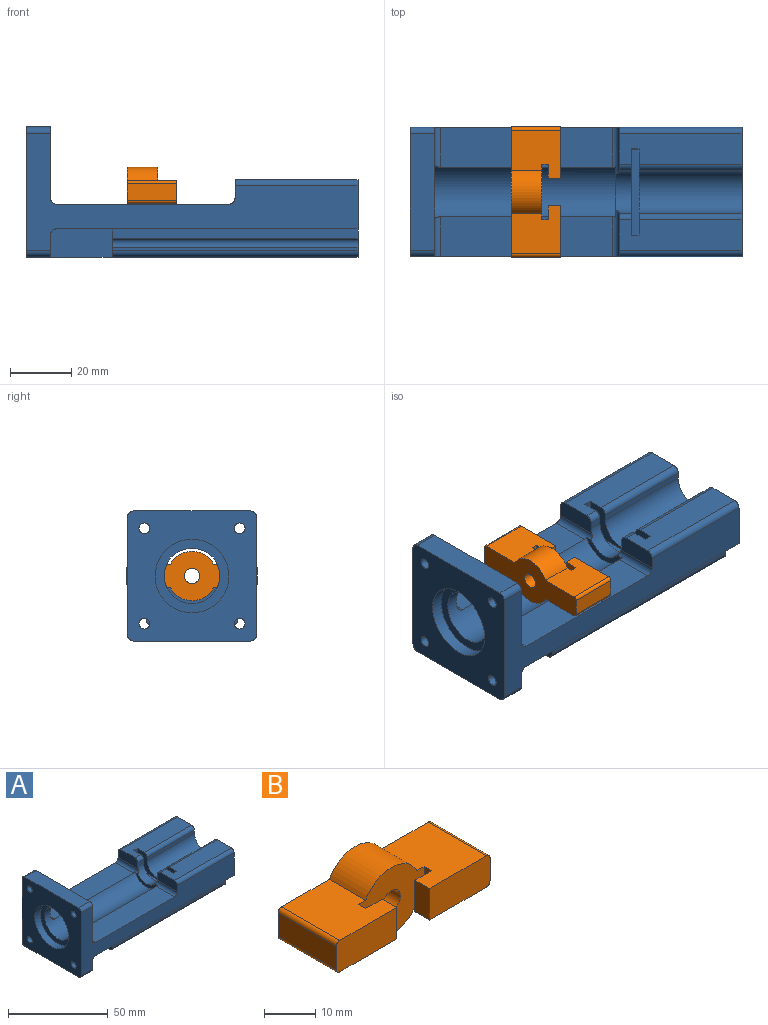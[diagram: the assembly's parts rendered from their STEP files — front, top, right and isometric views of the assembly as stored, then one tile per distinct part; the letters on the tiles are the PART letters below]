
ASSEMBLY  parts=2 mates=1
PART A: 73 faces, bbox 108x42x42.3 mm
  f0: plane 56x12.94mm, normal (0,0,1), area 724.5mm2, adj f8,f9,f27,f70
  f1: plane 56x12.94mm, normal (0,0,1), area 724.5mm2, adj f6,f7,f28,f70
  f2: plane 4x0.52mm, normal (0,0,-1), area 2.1mm2, adj f5,f21,f34,f72
  f3: plane 4x0.52mm, normal (0,0,-1), area 2.1mm2, adj f4,f21,f34,f72
  f4: plane 4x0.59mm, normal (0,1,0), area 2.4mm2, adj f3,f21,f34,f70
  f5: plane 4x0.59mm, normal (0,-1,0), area 2.4mm2, adj f2,f21,f34,f70
  f6: cylinder r=2mm len=15.08mm, axis (0,-1,0), area 44.2mm2, adj f1,f17,f20,f28,f70,f71
  f7: cylinder r=2mm len=12.94mm, axis (0,-1,0), area 39.5mm2, adj f1,f21,f28,f70
  f8: cylinder r=2mm len=15.08mm, axis (0,-1,0), area 44.2mm2, adj f0,f17,f19,f27,f70,f71
  f9: cylinder r=2mm len=12.94mm, axis (0,-1,0), area 39.5mm2, adj f0,f21,f27,f70
  f10: plane 98.02x10.18mm, normal (0,0,-1), area 677.5mm2, adj f12,f22,f28,f48,f50,f52,f53,f54
  f11: plane 11.8x7.15mm, normal (1,0,0), area 74.2mm2, adj f25,f27,f31,f51,f61,f63,f67
  f12: plane 9.15x4.18mm, normal (-1,0,0), area 34.4mm2, adj f10,f25,f46,f47,f48,f50,f56
  f13: plane 98.02x11.8mm, normal (0,0,-1), area 706.7mm2, adj f22,f27,f43,f49,f51,f61,f62,f63
  f14: plane 40x10mm, normal (0,0,1), area 387.5mm2, adj f19,f22,f38,f40,f41,f57,f59,f69
  f15: plane 40x10mm, normal (0,0,1), area 387.5mm2, adj f20,f22,f38,f39,f40,f58,f60,f66
  f16: plane 4x2mm, normal (0,1,0), area 8mm2, adj f17,f19,f40,f59
  f17: cylinder r=7mm len=14mm, axis (-1,0,0), area 103.2mm2, adj f6,f8,f16,f18,f19,f20,f40,f71
  f18: plane 4x2mm, normal (0,-1,0), area 8mm2, adj f17,f20,f40,f60
  f19: plane 14.29x6mm, normal (-1,0,0), area 82.5mm2, adj f8,f14,f16,f17,f27,f59,f69
  f20: plane 14.29x6mm, normal (-1,0,0), area 82.5mm2, adj f6,f15,f17,f18,f28,f60,f66
  f21: plane 42x23.15mm, normal (1,0,0), area 788.1mm2, adj f2,f3,f4,f5,f7,f9,f23,f27
  f22: plane 42x25.15mm, normal (1,0,0), area 802.4mm2, adj f10,f13,f14,f15,f25,f27,f28,f35
  f23: plane 38x8mm, normal (0,0,1), area 304mm2, adj f21,f24,f65,f68
  f24: plane 42.3x42mm, normal (-1,0,0), area 1282.3mm2, adj f23,f25,f27,f28,f29,f30,f31,f32
  f25: plane 108x38mm, normal (0,0,-1), area 2784.4mm2, adj f11,f12,f22,f24,f26,f49,f50,f51
  f26: plane 10.18x7.15mm, normal (1,0,0), area 62.6mm2, adj f25,f28,f32,f50,f52,f54,f64
  f27: plane 108x38.3mm, normal (0,-1,0), area 1349mm2, adj f0,f8,f9,f11,f13,f19,f21,f22
  f28: plane 108x38.3mm, normal (0,1,0), area 1349mm2, adj f1,f6,f7,f10,f20,f21,f22,f24
  f29: cylinder r=1.75mm len=8mm, axis (-1,0,0), area 88mm2, adj f21,f24
  f30: cylinder r=1.75mm len=8mm, axis (-1,0,0), area 88mm2, adj f21,f24
  f31: cylinder r=1.75mm len=8mm, axis (-1,0,0), area 88mm2, adj f11,f24,f62
  f32: cylinder r=1.75mm len=8mm, axis (-1,0,0), area 88mm2, adj f24,f26,f53
  f33: cylinder r=12mm len=24mm, axis (-1,0,0), area 301.6mm2, adj f24,f34
  f34: plane 24x24mm, normal (-1,0,0), area 197.6mm2, adj f2,f3,f4,f5,f33,f70,f72
  f35: plane 33.5x2mm, normal (0,1,0), area 67mm2, adj f22,f36,f38,f57
  f36: cylinder r=7mm len=33.5mm, axis (-1,0,0), area 736.7mm2, adj f22,f35,f37,f38
  f37: plane 33.5x2mm, normal (0,-1,0), area 67mm2, adj f22,f36,f38,f58
  f38: plane 28x12mm, normal (-1,0,0), area 201.3mm2, adj f14,f15,f35,f36,f37,f39,f41,f42
  f39: plane 12x2.5mm, normal (0,-1,0), area 30mm2, adj f15,f38,f40,f42
  f40: plane 28x12mm, normal (1,0,0), area 201.3mm2, adj f14,f15,f16,f17,f18,f39,f41,f42
  f41: plane 12x2.5mm, normal (0,1,0), area 30mm2, adj f14,f38,f40,f42
  f42: plane 28x2.5mm, normal (0,0,1), area 70mm2, adj f38,f39,f40,f41
  f43: plane 80x3.18mm, normal (0,-1,0), area 254.6mm2, adj f13,f22,f44,f49
  f44: cylinder r=1.5mm len=80mm, axis (1,0,0), area 300.5mm2, adj f22,f43,f45,f49
  f45: plane 80x1.12mm, normal (0,-1,0), area 89.9mm2, adj f22,f44,f49,f55
  f46: plane 80x1.12mm, normal (0,1,0), area 89.9mm2, adj f12,f22,f47,f56
  f47: cylinder r=1.5mm len=80mm, axis (1,0,0), area 300.5mm2, adj f12,f22,f46,f48
  f48: plane 80x3.18mm, normal (0,1,0), area 254.6mm2, adj f10,f12,f22,f47
  f49: plane 9.15x5.8mm, normal (-1,0,0), area 49.3mm2, adj f13,f25,f43,f44,f45,f51,f55
  f50: plane 20x9.15mm, normal (0,1,0), area 182.1mm2, adj f10,f12,f25,f26,f54
  f51: plane 20x9.15mm, normal (0,-1,0), area 182.1mm2, adj f11,f13,f25,f49,f61
  f52: cylinder r=2mm len=4.6mm, axis (0,-1,0), area 14.4mm2, adj f10,f26,f28,f53
  f53: bspline ~2.27x2.16mm, area 5.4mm2, adj f10,f32,f52,f54
  f54: cylinder r=2mm len=3.78mm, axis (0,-1,0), area 11.9mm2, adj f10,f26,f50,f53
  f55: cylinder r=2mm len=80mm, axis (1,0,0), area 251.3mm2, adj f22,f25,f45,f49
  f56: cylinder r=2mm len=80mm, axis (-1,0,0), area 251.3mm2, adj f12,f22,f25,f46
  f57: cylinder r=2mm len=33.5mm, axis (-1,0,0), area 105.2mm2, adj f14,f22,f35,f38
  f58: cylinder r=2mm len=33.5mm, axis (1,0,0), area 105.2mm2, adj f15,f22,f37,f38
  f59: cylinder r=2mm len=4mm, axis (-1,0,0), area 12.6mm2, adj f14,f16,f19,f40
  f60: cylinder r=2mm len=4mm, axis (1,0,0), area 12.6mm2, adj f15,f18,f20,f40
  f61: cylinder r=2mm len=5.4mm, axis (0,-1,0), area 17mm2, adj f11,f13,f51,f62
  f62: bspline ~2.27x2.16mm, area 5.4mm2, adj f13,f31,f61,f63
  f63: cylinder r=2mm len=4.6mm, axis (0,-1,0), area 14.4mm2, adj f11,f13,f27,f62
  f64: cylinder r=2mm len=8mm, axis (1,0,0), area 25.1mm2, adj f24,f25,f26,f28
  f65: cylinder r=2mm len=8mm, axis (-1,0,0), area 25.1mm2, adj f21,f23,f24,f28
  f66: cylinder r=2mm len=40mm, axis (-1,0,0), area 125.7mm2, adj f15,f20,f22,f28
  f67: cylinder r=2mm len=8mm, axis (-1,0,0), area 25.1mm2, adj f11,f24,f25,f27
  f68: cylinder r=2mm len=8mm, axis (1,0,0), area 25.1mm2, adj f21,f23,f24,f27
  f69: cylinder r=2mm len=40mm, axis (1,0,0), area 125.7mm2, adj f14,f19,f22,f27
  f70: cylinder r=9mm len=63mm, axis (-1,0,0), area 1343.3mm2, adj f0,f1,f4,f5,f6,f7,f8,f9
  f71: plane 16.38x5.27mm, normal (-1,0,0), area 34.7mm2, adj f6,f8,f17,f70
  f72: cylinder r=9mm len=12.96mm, axis (-1,0,0), area 57.9mm2, adj f2,f3,f21,f34
PART B: 23 faces, bbox 42.3x16x16 mm
  f0: plane 16x15.65mm, normal (0,0,1), area 215.7mm2, adj f2,f8,f9,f10,f11,f12,f19,f21
  f1: plane 16x15.65mm, normal (0,0,-1), area 215.7mm2, adj f2,f8,f9,f10,f11,f12,f17,f20
  f2: plane 42.3x16mm, normal (0,1,0), area 382.4mm2, adj f0,f1,f3,f13,f14,f15,f16,f17
  f3: plane 16x5.5mm, normal (-1,0,0), area 88mm2, adj f2,f4,f16,f18
  f4: plane 16.65x7.5mm, normal (0,-1,0), area 124.4mm2, adj f3,f5,f14,f15,f16,f18
  f5: plane 7.5x4mm, normal (1,0,0), area 30mm2, adj f4,f6,f14,f15
  f6: plane 7.5x4.5mm, normal (0,1,0), area 33.7mm2, adj f5,f7,f14,f15
  f7: plane 7.5x2mm, normal (1,0,0), area 15mm2, adj f6,f8,f14,f15
  f8: plane 18x16mm, normal (0,-1,0), area 201mm2, adj f0,f1,f7,f9,f14,f15,f20,f21
  f9: plane 7.5x2mm, normal (-1,0,0), area 15mm2, adj f0,f1,f8,f10
  f10: plane 7.5x4.5mm, normal (0,1,0), area 33.7mm2, adj f0,f1,f9,f11
  f11: plane 7.5x4mm, normal (-1,0,0), area 30mm2, adj f0,f1,f10,f12
  f12: plane 16.65x7.5mm, normal (0,-1,0), area 124.4mm2, adj f0,f1,f11,f13,f17,f19
  f13: plane 16x5.5mm, normal (1,0,0), area 88mm2, adj f2,f12,f17,f19
  f14: plane 16x15.65mm, normal (0,0,1), area 215.7mm2, adj f2,f4,f5,f6,f7,f8,f18,f21
  f15: plane 16x15.65mm, normal (0,0,-1), area 215.7mm2, adj f2,f4,f5,f6,f7,f8,f16,f20
  f16: cylinder r=1mm len=16mm, axis (0,-1,0), area 25.1mm2, adj f2,f3,f4,f15
  f17: cylinder r=1mm len=16mm, axis (0,1,0), area 25.1mm2, adj f1,f2,f12,f13
  f18: cylinder r=1mm len=16mm, axis (0,1,0), area 25.1mm2, adj f2,f3,f4,f14
  f19: cylinder r=1mm len=16mm, axis (0,-1,0), area 25.1mm2, adj f0,f2,f12,f13
  f20: cylinder r=8mm len=14.13mm, axis (0,1,0), area 173.3mm2, adj f1,f2,f8,f15
  f21: cylinder r=8mm len=14.13mm, axis (0,1,0), area 173.3mm2, adj f0,f2,f8,f14
  f22: cylinder r=2.5mm len=10mm, axis (0,1,0), area 157.1mm2, adj f2,f8
PLACE A t=(-10.63,-14.75,-22.65)mm
PLACE B rot(axis=(0,0,1),90deg) t=(22.29,-14.75,-22.65)mm
MATE slider B.f22 <-> A.f33  axis (1,0,0) through (32.29,-14.75,-22.65)mm
